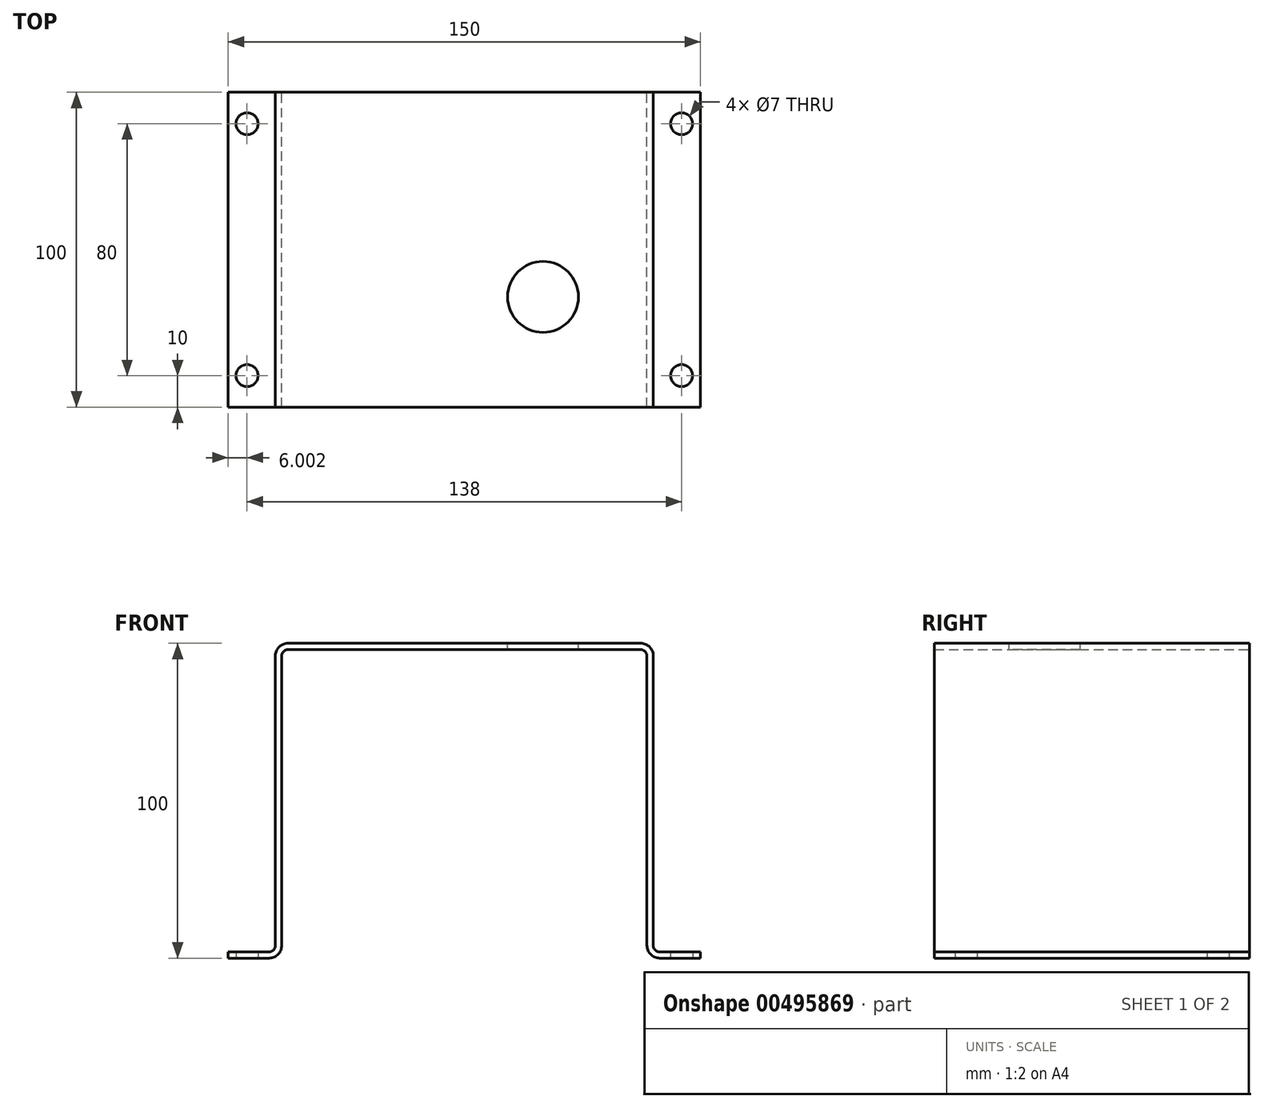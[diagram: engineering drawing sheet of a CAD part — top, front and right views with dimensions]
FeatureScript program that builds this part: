
annotation { "Feature Type Name" : "Feature", "Feature Type Description" : "" }
export const myFeature = defineFeature(function(context is Context, id is Id, definition is map)
    precondition{}
    {
        {
            var Q0;
            Q0=qCreatedBy(makeId("Front.planeOp"),FACE);
            var sketch = newSketch(context, id + "F0", { "sketchPlane" : qUnion([Q0])});
            skLineSegment(sketch, "E0", {"start": v(-106.89, 0) * mm, "end": v(-93.89, 0) * mm});
            skLineSegment(sketch, "E1", {"start": v(-91.89, 2) * mm, "end": v(-91.89, 94) * mm});
            skLineSegment(sketch, "E2", {"start": v(-87.89, 98) * mm, "end": v(24.11, 98) * mm});
            skLineSegment(sketch, "E3", {"start": v(28.11, 94) * mm, "end": v(28.11, 2) * mm});
            skLineSegment(sketch, "E4", {"start": v(30.11, 0) * mm, "end": v(43.11, 0) * mm});
            skPoint(sketch, "E5.visualSharp", {"position": v(-91.89, 0) * mm});
            skArc(sketch, "E5.filletArc", {"start": v(-93.89, 0) * mm, "mid": v(-92.47, 0.59) * mm, "end": v(-91.89, 2) * mm});
            skPoint(sketch, "E6.visualSharp", {"position": v(-91.89, 98) * mm});
            skArc(sketch, "E6.filletArc", {"start": v(-87.89, 98) * mm, "mid": v(-90.72, 96.83) * mm, "end": v(-91.89, 94) * mm});
            skPoint(sketch, "E7.visualSharp", {"position": v(28.11, 98) * mm});
            skArc(sketch, "E7.filletArc", {"start": v(28.11, 94) * mm, "mid": v(26.94, 96.83) * mm, "end": v(24.11, 98) * mm});
            skPoint(sketch, "E8.visualSharp", {"position": v(28.11, 0) * mm});
            skArc(sketch, "E8.filletArc", {"start": v(28.11, 2) * mm, "mid": v(28.7, 0.59) * mm, "end": v(30.11, 0) * mm});
            skLineSegment(sketch, "E9.0", {"start": v(30.11, -2) * mm, "end": v(43.11, -2) * mm});
            skArc(sketch, "E9.1", {"start": v(26.11, 2) * mm, "mid": v(27.28, -0.83) * mm, "end": v(30.11, -2) * mm});
            skLineSegment(sketch, "E9.2", {"start": v(26.11, 94) * mm, "end": v(26.11, 2) * mm});
            skLineSegment(sketch, "E9.3", {"start": v(-106.89, -2) * mm, "end": v(-93.89, -2) * mm});
            skArc(sketch, "E9.4", {"start": v(-93.89, -2) * mm, "mid": v(-91.06, -0.83) * mm, "end": v(-89.89, 2) * mm});
            skLineSegment(sketch, "E9.5", {"start": v(-89.89, 2) * mm, "end": v(-89.89, 94) * mm});
            skLineSegment(sketch, "E9.6", {"start": v(-87.89, 96) * mm, "end": v(24.11, 96) * mm});
            skPoint(sketch, "E10.visualSharp", {"position": v(-89.89, 96) * mm});
            skArc(sketch, "E10.filletArc", {"start": v(-87.89, 96) * mm, "mid": v(-89.3, 95.41) * mm, "end": v(-89.89, 94) * mm});
            skPoint(sketch, "E11.visualSharp", {"position": v(26.11, 96) * mm});
            skArc(sketch, "E11.filletArc", {"start": v(26.11, 94) * mm, "mid": v(25.53, 95.41) * mm, "end": v(24.11, 96) * mm});
            skLineSegment(sketch, "E12", {"start": v(-106.89, 0) * mm, "end": v(-106.89, -2) * mm});
            skLineSegment(sketch, "E13", {"start": v(43.11, 0) * mm, "end": v(43.11, -2) * mm});
            skSolve(sketch);
        }
        {
            var Q0;
            Q0=makeQuery(id+"F0.imprint","IMPRINT",FACE,{"disambiguationData":[TD([[makeQuery(id+"F0.imprint","IMPRINT",EDGE,{"derivedFrom":sQuery(id+"F0.wireOp",EDGE,"E0")}),-1.0]])]});
            extrude(context, id + "F1", {"entities" : qUnion([Q0]), "depth" : 100 * mm, "offsetDistance" : 25 * mm});
        }
        {
            var Q0;
            Q0=makeQuery(id+"F1.opExtrude","SWEPT_FACE",FACE,{"disambiguationData":[OSD([sQuery(id+"F0.wireOp",EDGE,"E2")])]});
            var sketch = newSketch(context, id + "F2", { "sketchPlane" : qUnion([Q0])});
            skCircle(sketch, "E14", {"center": v(-6.89, -65) * mm, "radius": 11.25 * mm});
            skSolve(sketch);
        }
        {
            var Q0;
            Q0=makeQuery(id+"F2.imprint","IMPRINT",FACE,{"disambiguationData":[TD([[makeQuery(id+"F2.imprint","IMPRINT",EDGE,{"derivedFrom":sQuery(id+"F2.wireOp",EDGE,"E14")}),1.0]])]});
            extrude(context, id + "F3", {"entities" : qUnion([Q0]), "operationType" : NewBodyOperationType.REMOVE, "oppositeDirection" : true, "depth" : 25 * mm, "offsetDistance" : 25 * mm});
        }
        {
            var Q0;
            Q0=makeQuery(id+"F1.opExtrude","SWEPT_FACE",FACE,{"disambiguationData":[OSD([sQuery(id+"F0.wireOp",EDGE,"E9.0")])]});
            var sketch = newSketch(context, id + "F4", { "sketchPlane" : qUnion([Q0])});
            skCircle(sketch, "E15", {"center": v(37.11, 90) * mm, "radius": 3.5 * mm});
            skCircle(sketch, "E16", {"center": v(37.11, 10) * mm, "radius": 3.5 * mm});
            skCircle(sketch, "E17", {"center": v(-100.89, 90) * mm, "radius": 3.5 * mm});
            skCircle(sketch, "E18", {"center": v(-100.89, 10) * mm, "radius": 3.5 * mm});
            skSolve(sketch);
        }
        {
            var Q0;
            Q0=makeQuery(id+"F4.imprint","IMPRINT",FACE,{"disambiguationData":[TD([[makeQuery(id+"F4.imprint","IMPRINT",EDGE,{"derivedFrom":sQuery(id+"F4.wireOp",EDGE,"E15")}),1.0]])]});
            var Q1;
            Q1=makeQuery(id+"F4.imprint","IMPRINT",FACE,{"disambiguationData":[TD([[makeQuery(id+"F4.imprint","IMPRINT",EDGE,{"derivedFrom":sQuery(id+"F4.wireOp",EDGE,"E16")}),1.0]])]});
            var Q2;
            Q2=makeQuery(id+"F4.imprint","IMPRINT",FACE,{"disambiguationData":[TD([[makeQuery(id+"F4.imprint","IMPRINT",EDGE,{"derivedFrom":sQuery(id+"F4.wireOp",EDGE,"E18")}),1.0]])]});
            var Q3;
            Q3=makeQuery(id+"F4.imprint","IMPRINT",FACE,{"disambiguationData":[TD([[makeQuery(id+"F4.imprint","IMPRINT",EDGE,{"derivedFrom":sQuery(id+"F4.wireOp",EDGE,"E17")}),1.0]])]});
            extrude(context, id + "F5", {"entities" : qUnion([Q0, Q1, Q2, Q3]), "operationType" : NewBodyOperationType.REMOVE, "oppositeDirection" : true, "depth" : 25 * mm, "offsetDistance" : 25 * mm});
        }
    });
